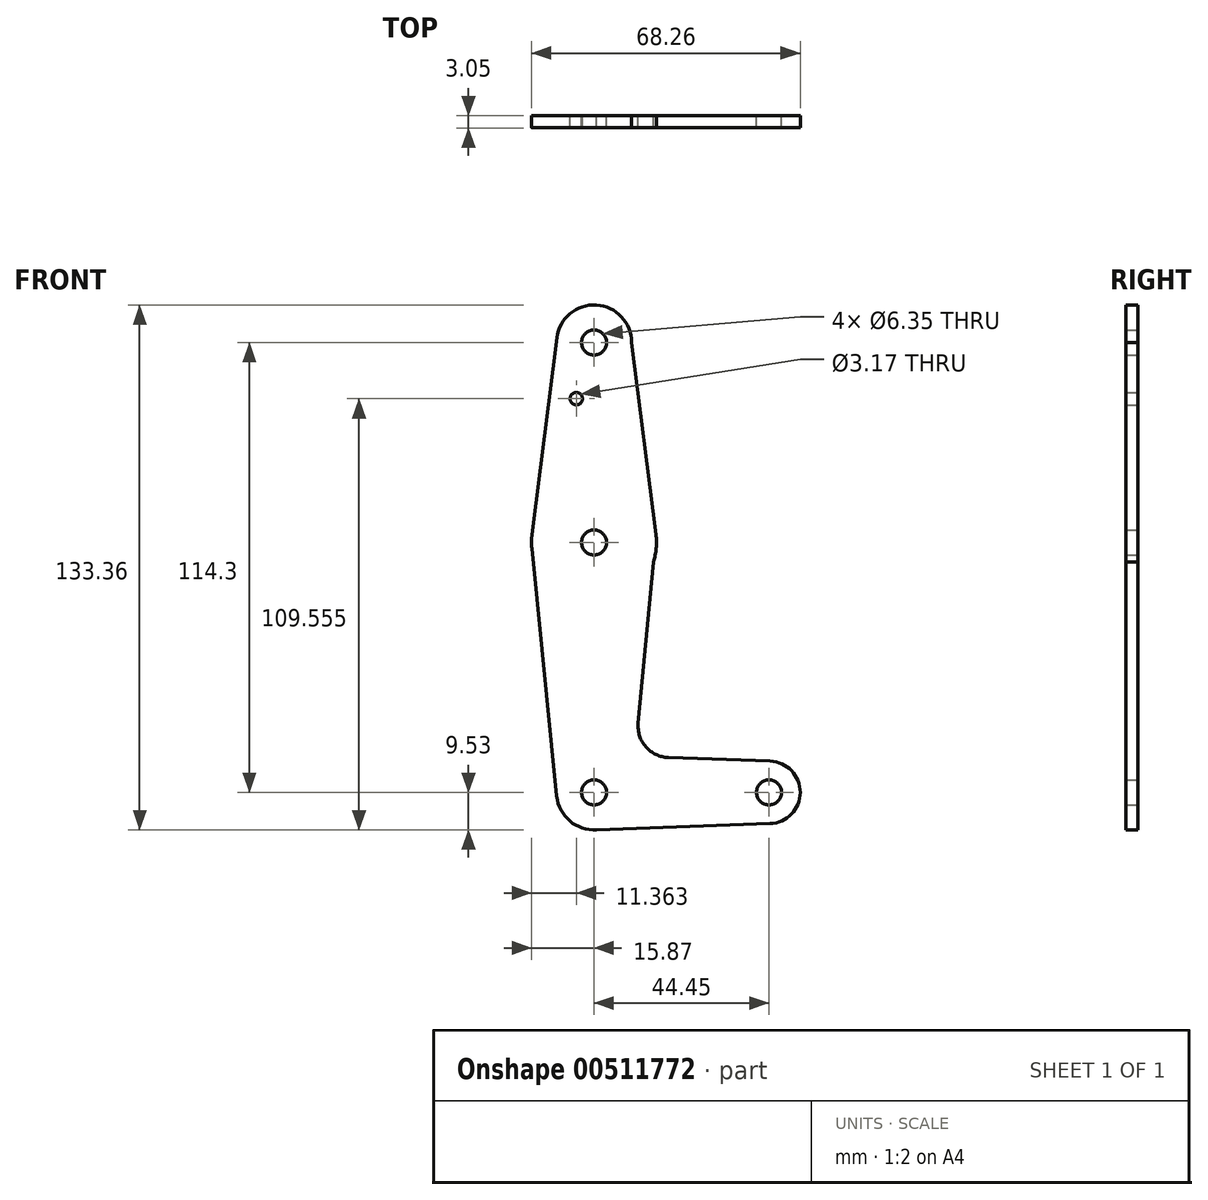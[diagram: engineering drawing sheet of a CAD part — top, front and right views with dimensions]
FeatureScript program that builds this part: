
annotation { "Feature Type Name" : "Feature", "Feature Type Description" : "" }
export const myFeature = defineFeature(function(context is Context, id is Id, definition is map)
    precondition{}
    {
        {
            var Q0;
            Q0=qCreatedBy(makeId("Front.planeOp"),FACE);
            var sketch = newSketch(context, id + "F0", { "sketchPlane" : qUnion([Q0])});
            skCircle(sketch, "E0", {"center": v(0, 0) * mm, "radius": 9.53 * mm});
            skCircle(sketch, "E1", {"center": v(0, 63.5) * mm, "radius": 15.88 * mm});
            skCircle(sketch, "E2", {"center": v(0, 114.3) * mm, "radius": 9.53 * mm});
            skCircle(sketch, "E3", {"center": v(44.45, 0) * mm, "radius": 7.94 * mm});
            skLineSegment(sketch, "E4", {"start": v(44.45, 0) * mm, "end": v(0, 0) * mm, "construction": true});
            skLineSegment(sketch, "E5", {"start": v(0, 0) * mm, "end": v(0, 63.5) * mm, "construction": true});
            skLineSegment(sketch, "E6", {"start": v(0, 114.3) * mm, "end": v(0, 63.5) * mm, "construction": true});
            skLineSegment(sketch, "E7", {"start": v(-9.45, 115.5) * mm, "end": v(-15.75, 65.48) * mm});
            skLineSegment(sketch, "E8", {"start": v(9.52, 114.3) * mm, "end": v(15.75, 65.5) * mm});
            skLineSegment(sketch, "E9", {"start": v(15.75, 65.5) * mm, "end": v(11.22, 17.55) * mm});
            skLineSegment(sketch, "E10", {"start": v(18.85, 8.86) * mm, "end": v(44.73, 7.93) * mm});
            skLineSegment(sketch, "E11", {"start": v(0, -9.53) * mm, "end": v(44.73, -7.93) * mm});
            skCircle(sketch, "E12", {"center": v(0, 114.3) * mm, "radius": 3.18 * mm});
            skCircle(sketch, "E13", {"center": v(0, 63.5) * mm, "radius": 3.18 * mm});
            skCircle(sketch, "E14", {"center": v(0, 0) * mm, "radius": 3.18 * mm});
            skCircle(sketch, "E15", {"center": v(44.45, 0) * mm, "radius": 3.18 * mm});
            skCircle(sketch, "E16", {"center": v(-4.5, 100.03) * mm, "radius": 1.59 * mm});
            skArc(sketch, "E17.filletArc", {"start": v(11.22, 17.55) * mm, "mid": v(13.16, 11.56) * mm, "end": v(18.85, 8.86) * mm});
            skLineSegment(sketch, "E18", {"start": v(-15.8, 61.91) * mm, "end": v(-9.48, -0.95) * mm});
            skSolve(sketch);
        }
        {
            var Q0;
            Q0 = qSketchRegion(id + "F0", true);
            extrude(context, id + "F1", {"entities" : qUnion([Q0]), "depth" : 3.05 * mm});
        }
    });
